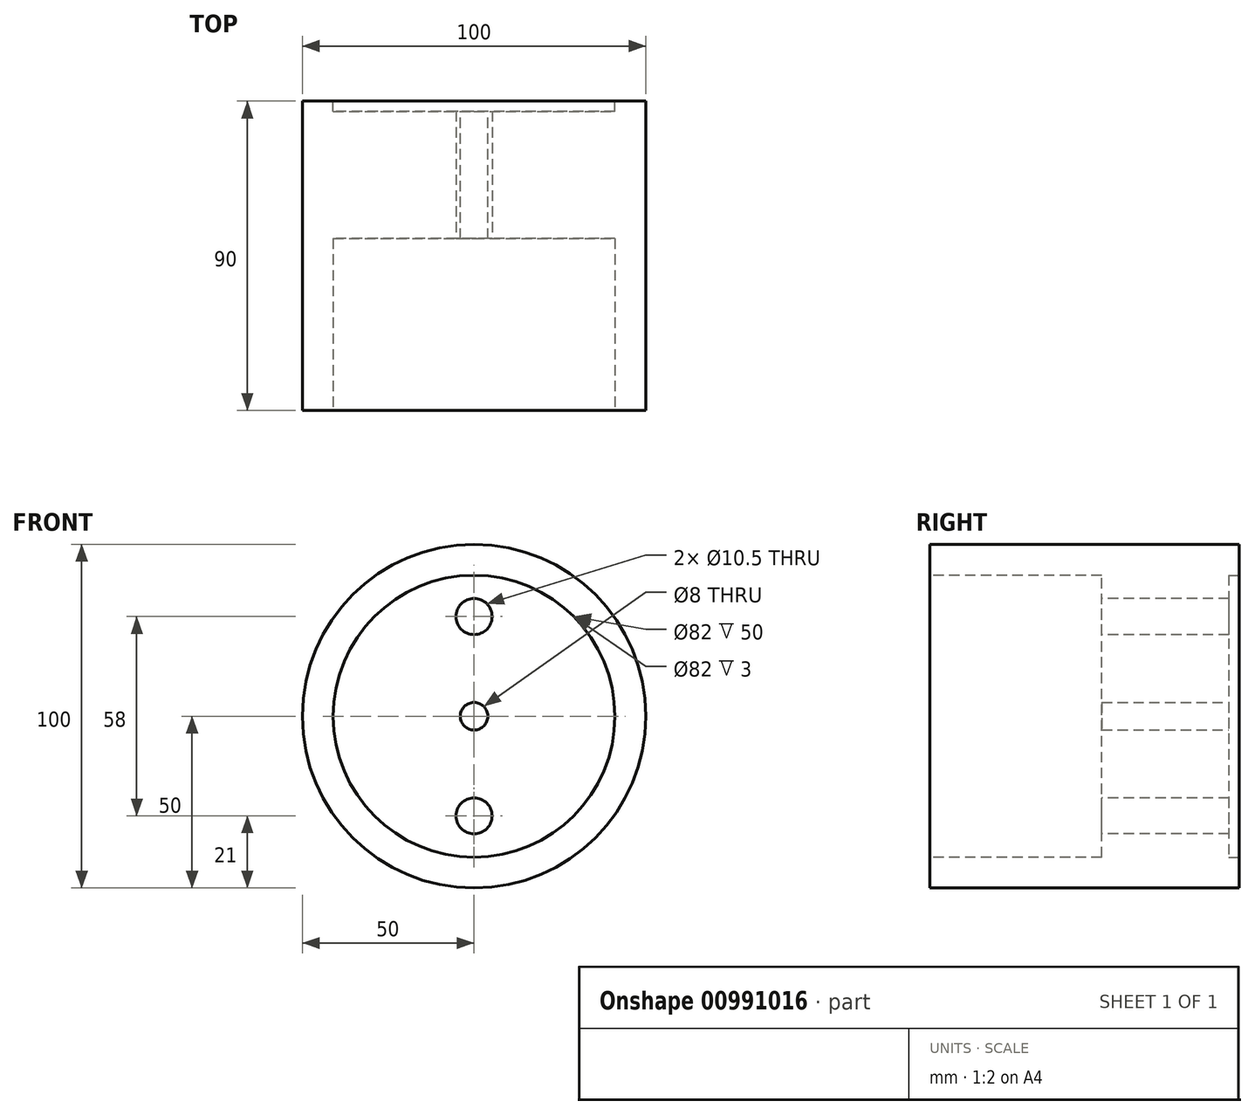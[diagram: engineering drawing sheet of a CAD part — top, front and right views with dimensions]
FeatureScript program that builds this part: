
annotation { "Feature Type Name" : "Feature", "Feature Type Description" : "" }
export const myFeature = defineFeature(function(context is Context, id is Id, definition is map)
    precondition{}
    {
        {
            var Q0;
            Q0=qCreatedBy(makeId("Front.planeOp"),FACE);
            var sketch = newSketch(context, id + "F0", { "sketchPlane" : qUnion([Q0])});
            skCircle(sketch, "E0", {"center": v(0, 0) * mm, "radius": 50 * mm});
            skSolve(sketch);
        }
        {
            var Q0;
            Q0=makeQuery(id+"F0.imprint","IMPRINT",FACE,{"disambiguationData":[TD([[makeQuery(id+"F0.imprint","IMPRINT",EDGE,{"derivedFrom":sQuery(id+"F0.wireOp",EDGE,"E0")}),1.0]])]});
            extrude(context, id + "F1", {"entities" : qUnion([Q0]), "depth" : 90 * mm, "offsetDistance" : 25 * mm});
        }
        {
            var Q0;
            Q0=makeQuery(id+"F1.opExtrude","CAP_FACE",FACE,{"disambiguationData":[OSD([sQuery(id+"F0.wireOp",EDGE,"E0")])],"isStart":false});
            var sketch = newSketch(context, id + "F2", { "sketchPlane" : qUnion([Q0])});
            skCircle(sketch, "E1", {"center": v(0, 0) * mm, "radius": 41 * mm});
            skSolve(sketch);
        }
        {
            var Q0;
            Q0=makeQuery(id+"F2.imprint","IMPRINT",FACE,{"disambiguationData":[TD([[makeQuery(id+"F2.imprint","IMPRINT",EDGE,{"derivedFrom":sQuery(id+"F2.wireOp",EDGE,"E1")}),1.0]])]});
            extrude(context, id + "F3", {"entities" : qUnion([Q0]), "operationType" : NewBodyOperationType.REMOVE, "oppositeDirection" : true, "depth" : 50 * mm, "offsetDistance" : 25 * mm});
        }
        {
            var Q0;
            Q0=makeQuery(id+"F1.opExtrude","CAP_FACE",FACE,{"disambiguationData":[OSD([sQuery(id+"F0.wireOp",EDGE,"E0")])],"isStart":true});
            var sketch = newSketch(context, id + "F4", { "sketchPlane" : qUnion([Q0])});
            skCircle(sketch, "E2", {"center": v(0, 0) * mm, "radius": 4 * mm});
            skSolve(sketch);
        }
        {
            var Q0;
            Q0=makeQuery(id+"F4.imprint","IMPRINT",FACE,{"disambiguationData":[TD([[makeQuery(id+"F4.imprint","IMPRINT",EDGE,{"derivedFrom":sQuery(id+"F4.wireOp",EDGE,"E2")}),1.0]])]});
            extrude(context, id + "F5", {"entities" : qUnion([Q0]), "operationType" : NewBodyOperationType.REMOVE, "oppositeDirection" : true, "depth" : 151 * mm, "offsetDistance" : 25 * mm});
        }
        {
            var Q0;
            Q0=makeQuery(id+"F1.opExtrude","CAP_FACE",FACE,{"disambiguationData":[OSD([sQuery(id+"F0.wireOp",EDGE,"E0")])],"isStart":true});
            var sketch = newSketch(context, id + "F6", { "sketchPlane" : qUnion([Q0])});
            skCircle(sketch, "E3", {"center": v(0, 0) * mm, "radius": 41 * mm});
            skSolve(sketch);
        }
        {
            var Q0;
            Q0=makeQuery(id+"F6.imprint","IMPRINT",FACE,{"disambiguationData":[TD([[makeQuery(id+"F6.imprint","IMPRINT",EDGE,{"derivedFrom":sQuery(id+"F6.wireOp",EDGE,"E3")}),1.0]])]});
            extrude(context, id + "F7", {"entities" : qUnion([Q0]), "operationType" : NewBodyOperationType.REMOVE, "oppositeDirection" : true, "depth" : 3 * mm, "offsetDistance" : 25 * mm});
        }
        {
            var Q0;
            Q0=makeQuery(id+"F3.boolean.opBoolean","COPY",FACE,{"derivedFrom":makeQuery(id+"F3.opExtrude","CAP_FACE",FACE,{"disambiguationData":[OSD([sQuery(id+"F2.wireOp",EDGE,"E1")])],"isStart":false})});
            var sketch = newSketch(context, id + "F8", { "sketchPlane" : qUnion([Q0])});
            skCircle(sketch, "E4", {"center": v(0, 29) * mm, "radius": 5.25 * mm});
            skCircle(sketch, "E5", {"center": v(0, -29) * mm, "radius": 5.25 * mm});
            skSolve(sketch);
        }
        {
            var Q0;
            Q0 = qSketchRegion(id + "F8", true);
            extrude(context, id + "F9", {"entities" : qUnion([Q0]), "operationType" : NewBodyOperationType.REMOVE, "oppositeDirection" : true, "depth" : 72 * mm, "offsetDistance" : 25 * mm});
        }
    });
